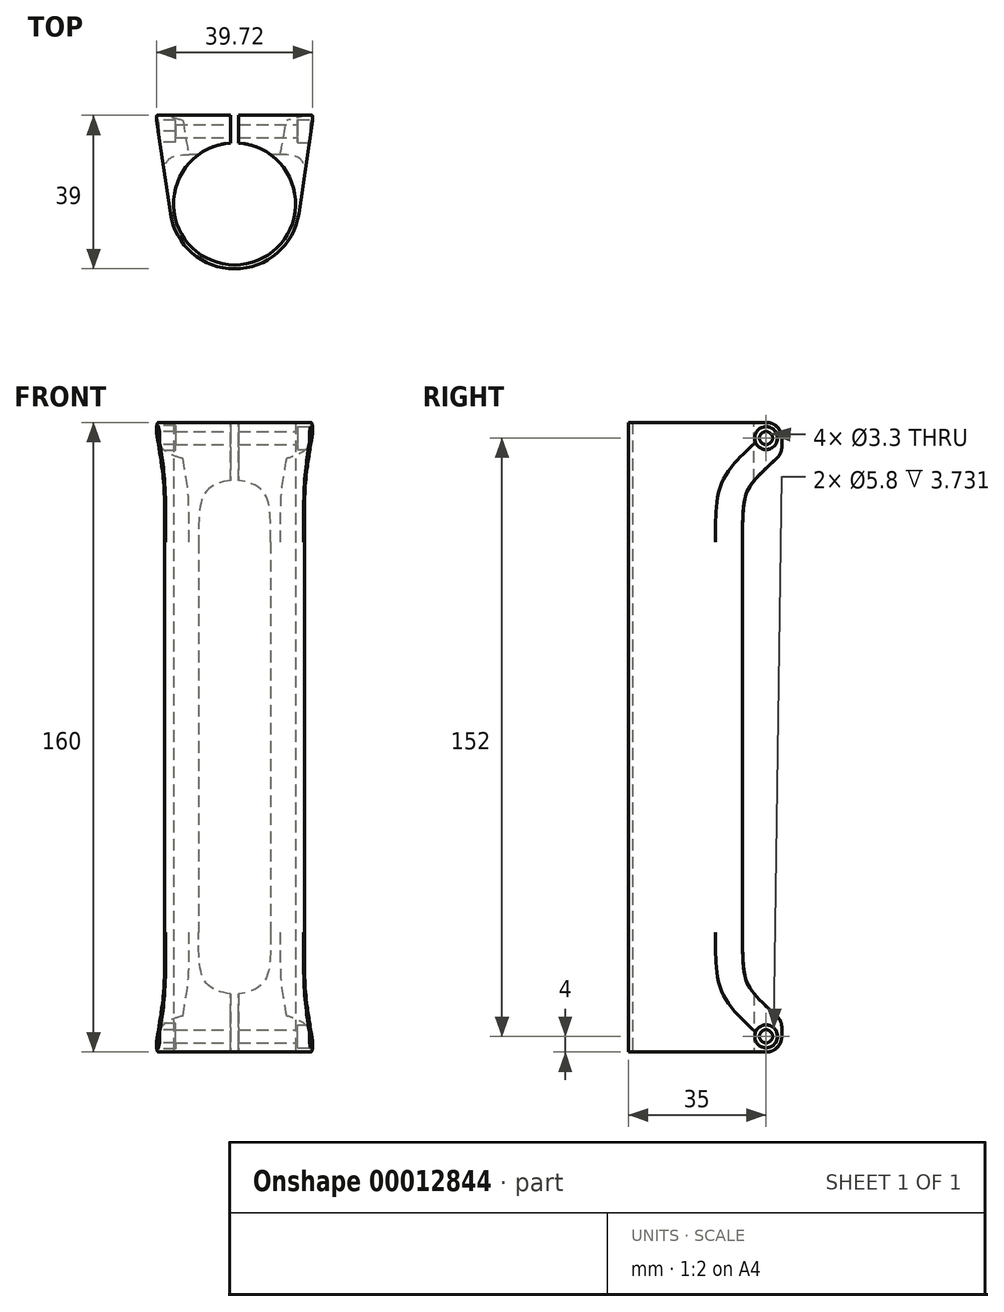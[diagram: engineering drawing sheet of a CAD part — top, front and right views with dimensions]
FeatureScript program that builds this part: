
annotation { "Feature Type Name" : "Feature", "Feature Type Description" : "" }
export const myFeature = defineFeature(function(context is Context, id is Id, definition is map)
    precondition{}
    {
        {
            var Q0;
            Q0=qCreatedBy(makeId("Top.planeOp"),FACE);
            var sketch = newSketch(context, id + "F0", { "sketchPlane" : qUnion([Q0])});
            skCircle(sketch, "E0", {"center": v(0, 0) * mm, "radius": 15.5 * mm});
            skSolve(sketch);
        }
        {
            var Q0;
            Q0=qCreatedBy(makeId("Top.planeOp"),FACE);
            var sketch = newSketch(context, id + "F1", { "sketchPlane" : qUnion([Q0])});
            skLineSegment(sketch, "E1", {"start": v(0, 22.5) * mm, "end": v(20, 22.5) * mm});
            skLineSegment(sketch, "E2", {"start": v(20, 22.5) * mm, "end": v(16.32, -2.4) * mm});
            skArc(sketch, "E3", {"start": v(0, -15.5) * mm, "mid": v(15.5, 0) * mm, "end": v(0, 15.5) * mm});
            skLineSegment(sketch, "E4", {"start": v(0, 15.5) * mm, "end": v(0, 22.5) * mm});
            skLineSegment(sketch, "E5", {"start": v(0, -15.5) * mm, "end": v(0, -16.5) * mm});
            skArc(sketch, "E6", {"start": v(0, -16.5) * mm, "mid": v(10.78, -12.5) * mm, "end": v(16.32, -2.4) * mm});
            skSolve(sketch);
        }
        {
            var Q0;
            Q0=makeQuery(id+"F1.imprint","IMPRINT",FACE,{"disambiguationData":[TD([[makeQuery(id+"F1.imprint","IMPRINT",EDGE,{"derivedFrom":sQuery(id+"F1.wireOp",EDGE,"E1")}),-1.0]])]});
            extrude(context, id + "F2", {"entities" : qUnion([Q0]), "depth" : 80 * mm});
        }
        {
            var Q0;
            Q0=makeQuery(id+"F2.opExtrude","SWEPT_BODY",BODY,{"disambiguationData":[OSD([sQuery(id+"F1.wireOp",EDGE,"E1"),sQuery(id+"F1.wireOp",EDGE,"E2"),sQuery(id+"F1.wireOp",EDGE,"6433310a-906e-4d0e-a87c-12e56682349a"),sQuery(id+"F1.wireOp",EDGE,"ec2daf9b-542c-445b-b6fd-9b136e921494"),sQuery(id+"F1.wireOp",EDGE,"E3"),sQuery(id+"F1.wireOp",EDGE,"E4")])]});
            var Q1;
            Q1=makeQuery(id+"F2.opExtrude","SWEPT_FACE",FACE,{"disambiguationData":[OSD([sQuery(id+"F1.wireOp",EDGE,"E4")])]});
            mirror(context, id + "F3", {"operationType" : NewBodyOperationType.ADD, "entities" : qUnion([Q0]), "mirrorPlane" : qUnion([Q1])});
        }
        {
            var Q0;
            Q0=qCreatedBy(makeId("Right.planeOp"),FACE);
            var sketch = newSketch(context, id + "F4", { "sketchPlane" : qUnion([Q0])});
            skLineSegment(sketch, "E7", {"start": v(22.5, 80) * mm, "end": v(22.5, 8) * mm});
            skLineSegment(sketch, "E8", {"start": v(12.5, 13.77) * mm, "end": v(12.5, 80) * mm});
            skLineSegment(sketch, "E9", {"start": v(22.5, 80) * mm, "end": v(12.5, 80) * mm});
            skLineSegment(sketch, "E10", {"start": v(15.5, 80) * mm, "end": v(15.5, 0) * mm, "construction": true});
            skLineSegment(sketch, "E11", {"start": v(12.5, 13.77) * mm, "end": v(22.5, 8) * mm});
            skSolve(sketch);
        }
        {
            var Q0;
            Q0=qSketchRegion(id+"F4",true);
            extrude(context, id + "F5", {"entities" : qUnion([Q0]), "operationType" : NewBodyOperationType.REMOVE, "endBound" : BoundingType.THROUGH_ALL, "oppositeDirection" : true, "depth" : 25 * mm, "hasSecondDirection" : true, "secondDirectionBound" : SecondDirectionBoundingType.THROUGH_ALL, "secondDirectionOppositeDirection" : false, "secondDirectionDepth" : 25 * mm});
        }
        {
            var Q0;
            Q0=makeQuery(id+"F5.boolean.opBoolean","COPY",EDGE,{"disambiguationData":[OD(1.0)],"derivedFrom":makeQuery(id+"F5.opExtrude","SWEPT_EDGE",EDGE,{"disambiguationData":[OSD([sQuery(id+"F4.wireOp",EDGE,"E8"),sQuery(id+"F4.wireOp",EDGE,"E11")])]})});
            fillet(context, id + "F6", {"entities" : qUnion([Q0]), "radius" : 30 * mm, "tangentPropagation" : true, "rho" : .75, "crossSection" : FilletCrossSection.CONIC, "allowEdgeOverflow" : false});
        }
        {
            var Q0;
            Q0=qCreatedBy(makeId("Right.planeOp"),FACE);
            var sketch = newSketch(context, id + "F7", { "sketchPlane" : qUnion([Q0])});
            skCircle(sketch, "E12", {"center": v(18.5, 4) * mm, "radius": 1.65 * mm});
            skLineSegment(sketch, "E13", {"start": v(18.5, 4) * mm, "end": v(18.5, 0) * mm, "construction": true});
            skLineSegment(sketch, "E14", {"start": v(18.5, 4) * mm, "end": v(22.5, 4) * mm, "construction": true});
            skLineSegment(sketch, "E15", {"start": v(18.5, 4) * mm, "end": v(12.5, 4) * mm, "construction": true});
            skSolve(sketch);
        }
        {
            var Q0;
            Q0=qSketchRegion(id+"F7",true);
            extrude(context, id + "F8", {"entities" : qUnion([Q0]), "operationType" : NewBodyOperationType.REMOVE, "endBound" : BoundingType.THROUGH_ALL, "oppositeDirection" : true, "depth" : 25 * mm, "hasSecondDirection" : true, "secondDirectionBound" : SecondDirectionBoundingType.THROUGH_ALL, "secondDirectionOppositeDirection" : false, "secondDirectionDepth" : 25 * mm});
        }
        {
            var Q0;
            Q0=qBodyType(qCreatedBy(id+"F10",EDGE),BodyType.WIRE);
            var Q1;
            Q1=qCreatedBy(makeId("Right.planeOp"),FACE);
            var Q2;
            Q2=makeQuery(id+"F2.opExtrude","CAP_VERTEX",VERTEX,{"disambiguationData":[OSD([sQuery(id+"F1.wireOp",EDGE,"E1"),sQuery(id+"F1.wireOp",EDGE,"E2")])],"isStart":true});
            cPlane(context, id + "F9", {"entities" : qUnion([Q0, Q1, Q2]), "cplaneType" : CPlaneType.PLANE_POINT, "offset" : 150 * mm, "width" : 150 * mm, "height" : 150 * mm});
        }
        {
            var Q0;
            Q0=qCreatedBy(id+"F9.planeOp",FACE);
            var sketch = newSketch(context, id + "F10", { "sketchPlane" : qUnion([Q0])});
            skCircle(sketch, "E16", {"center": v(18.5, 4) * mm, "radius": 2.9 * mm});
            skSolve(sketch);
        }
        {
            var Q0;
            Q0=qSketchRegion(id+"F10",true);
            extrude(context, id + "F11", {"entities" : qUnion([Q0]), "operationType" : NewBodyOperationType.REMOVE, "oppositeDirection" : true, "depth" : 4 * mm});
        }
        {
            var Q0;
            Q0=qBodyType(qCreatedBy(id+"F13",EDGE),BodyType.WIRE);
            var Q1;
            Q1=qCreatedBy(makeId("Right.planeOp"),FACE);
            var Q2;
            Q2=makeQuery(id+"F3.opPattern","COPY",VERTEX,{"derivedFrom":makeQuery(id+"F2.opExtrude","CAP_VERTEX",VERTEX,{"disambiguationData":[OSD([sQuery(id+"F1.wireOp",EDGE,"E1"),sQuery(id+"F1.wireOp",EDGE,"E2")])],"isStart":true}),"instanceName":"1"});
            cPlane(context, id + "F12", {"entities" : qUnion([Q0, Q1, Q2]), "cplaneType" : CPlaneType.PLANE_POINT, "offset" : 150 * mm, "width" : 150 * mm, "height" : 150 * mm});
        }
        {
            var Q0;
            Q0=qCreatedBy(id+"F12.planeOp",FACE);
            var sketch = newSketch(context, id + "F13", { "sketchPlane" : qUnion([Q0])});
            skLineSegment(sketch, "E17", {"start": v(15.7, 2.38) * mm, "end": v(15.7, 5.62) * mm});
            skLineSegment(sketch, "E18", {"start": v(15.7, 5.62) * mm, "end": v(18.5, 7.23) * mm});
            skLineSegment(sketch, "E19", {"start": v(18.5, 7.23) * mm, "end": v(21.3, 5.62) * mm});
            skLineSegment(sketch, "E20", {"start": v(21.3, 5.62) * mm, "end": v(21.3, 2.38) * mm});
            skLineSegment(sketch, "E21", {"start": v(21.3, 2.38) * mm, "end": v(18.5, 0.77) * mm});
            skLineSegment(sketch, "E22", {"start": v(18.5, 0.77) * mm, "end": v(15.7, 2.38) * mm});
            skCircle(sketch, "E23", {"center": v(18.5, 4) * mm, "radius": 3.23 * mm, "construction": true});
            skSolve(sketch);
        }
        {
            var Q0;
            Q0=makeQuery(id+"F13.imprint","IMPRINT",FACE,{"disambiguationData":[TD([[makeQuery(id+"F13.imprint","IMPRINT",EDGE,{"derivedFrom":sQuery(id+"F13.wireOp",EDGE,"E17")}),-1.0]])]});
            extrude(context, id + "F14", {"entities" : qUnion([Q0]), "operationType" : NewBodyOperationType.REMOVE, "depth" : 5 * mm});
        }
        {
            var Q0;
            {var subQ0=makeQuery(id+"F2.opExtrude","CAP_FACE",FACE,{"disambiguationData":[OSD([sQuery(id+"F1.wireOp",EDGE,"E1"),sQuery(id+"F1.wireOp",EDGE,"E2"),sQuery(id+"F1.wireOp",EDGE,"E3"),sQuery(id+"F1.wireOp",EDGE,"E4"),sQuery(id+"F1.wireOp",EDGE,"E5"),sQuery(id+"F1.wireOp",EDGE,"E6")])],"isStart":true});Q0=makeQuery(id+"F3.boolean.opBoolean","MERGE",FACE,{"derivedFrom":[subQ0,makeQuery(id+"F3.opPattern","COPY",FACE,{"derivedFrom":subQ0,"instanceName":"1"})]});}
            var sketch = newSketch(context, id + "F15", { "sketchPlane" : qUnion([Q0])});
            skLineSegment(sketch, "E24.bottom", {"start": v(1, -22.5) * mm, "end": v(-1, -22.5) * mm});
            skLineSegment(sketch, "E24.top", {"start": v(1, 0) * mm, "end": v(-1, 0) * mm});
            skLineSegment(sketch, "E24.left", {"start": v(1, -22.5) * mm, "end": v(1, 0) * mm});
            skLineSegment(sketch, "E24.right", {"start": v(-1, -22.5) * mm, "end": v(-1, 0) * mm});
            skSolve(sketch);
        }
        {
            var Q0;
            Q0=qSketchRegion(id+"F15",true);
            extrude(context, id + "F16", {"entities" : qUnion([Q0]), "operationType" : NewBodyOperationType.REMOVE, "endBound" : BoundingType.THROUGH_ALL, "oppositeDirection" : true, "depth" : 3 * mm});
        }
        {
            var Q0;
            Q0=makeQuery(id+"F5.boolean.opBoolean","INTERSECT",EDGE,{"derivedFrom":[makeQuery(id+"F2.opExtrude","SWEPT_FACE",FACE,{"disambiguationData":[OSD([sQuery(id+"F1.wireOp",EDGE,"E2")])]}),makeQuery(id+"F5.opExtrude","SWEPT_FACE",FACE,{"disambiguationData":[OSD([sQuery(id+"F4.wireOp",EDGE,"E8")])]})]});
            var Q1;
            Q1=makeQuery(id+"F5.boolean.opBoolean","INTERSECT",EDGE,{"derivedFrom":[makeQuery(id+"F3.opPattern","COPY",FACE,{"derivedFrom":makeQuery(id+"F2.opExtrude","SWEPT_FACE",FACE,{"disambiguationData":[OSD([sQuery(id+"F1.wireOp",EDGE,"E2")])]}),"instanceName":"1"}),makeQuery(id+"F5.opExtrude","SWEPT_FACE",FACE,{"disambiguationData":[OSD([sQuery(id+"F4.wireOp",EDGE,"E8")])]})]});
            fillet(context, id + "F17", {"entities" : qUnion([Q0, Q1]), "radius" : 6 * mm, "tangentPropagation" : true, "rho" : .6, "crossSection" : FilletCrossSection.CONIC, "allowEdgeOverflow" : false});
        }
        {
            var Q0;
            {var subQ0=sQuery(id+"F1.wireOp",EDGE,"E1");var subQ1=makeQuery(id+"F2.opExtrude","CAP_EDGE",EDGE,{"disambiguationData":[OSD([subQ0])],"isStart":true});var subQ2=sQuery(id+"F1.wireOp",EDGE,"E2");Q0=makeQuery(id+"F16.boolean.opBoolean","SPLIT",EDGE,{"disambiguationData":[TD([makeQuery(id+"F3.opPattern","COPY",FACE,{"derivedFrom":makeQuery(id+"F2.opExtrude","SWEPT_FACE",FACE,{"disambiguationData":[OSD([subQ2])]}),"instanceName":"1"})])],"derivedFrom":makeQuery(id+"F3.boolean.opBoolean","MERGE",EDGE,{"derivedFrom":[subQ1,makeQuery(id+"F3.opPattern","COPY",EDGE,{"derivedFrom":subQ1,"instanceName":"1"})]})});}
            var Q1;
            {var subQ0=sQuery(id+"F1.wireOp",EDGE,"E1");var subQ1=makeQuery(id+"F2.opExtrude","CAP_EDGE",EDGE,{"disambiguationData":[OSD([subQ0])],"isStart":true});var subQ3=sQuery(id+"F1.wireOp",EDGE,"E2");Q1=makeQuery(id+"F16.boolean.opBoolean","SPLIT",EDGE,{"disambiguationData":[TD([makeQuery(id+"F2.opExtrude","SWEPT_FACE",FACE,{"disambiguationData":[OSD([subQ3])]})])],"derivedFrom":makeQuery(id+"F3.boolean.opBoolean","MERGE",EDGE,{"derivedFrom":[subQ1,makeQuery(id+"F3.opPattern","COPY",EDGE,{"derivedFrom":subQ1,"instanceName":"1"})]})});}
            var Q2;
            {var subQ0=sQuery(id+"F4.wireOp",EDGE,"E8");var subQ1=sQuery(id+"F4.wireOp",EDGE,"E11");var subQ2=makeQuery(id+"F2.opExtrude","SWEPT_FACE",FACE,{"disambiguationData":[OSD([sQuery(id+"F1.wireOp",EDGE,"E1")])]});var subQ3=makeQuery(id+"F3.opPattern","COPY",FACE,{"derivedFrom":subQ2,"instanceName":"1"});Q2=makeQuery(id+"F16.boolean.opBoolean","SPLIT",EDGE,{"disambiguationData":[TD([makeQuery(id+"F2.opExtrude","SWEPT_FACE",FACE,{"disambiguationData":[OSD([sQuery(id+"F1.wireOp",EDGE,"E2")])]})])],"derivedFrom":makeQuery(id+"F6.opFillet","BLEND_EDGE",EDGE,{"blendedFrom":[makeQuery(id+"F5.boolean.opBoolean","COPY",EDGE,{"disambiguationData":[OD(1.0)],"derivedFrom":makeQuery(id+"F5.opExtrude","SWEPT_EDGE",EDGE,{"disambiguationData":[OSD([subQ0,subQ1])]})}),makeQuery(id+"F3.boolean.opBoolean","MERGE",FACE,{"derivedFrom":[subQ2,subQ3]})],"blendedInto":[makeQuery(id+"F3.boolean.opBoolean","MERGE",FACE,{"derivedFrom":[subQ2,subQ3]})]})});}
            var Q3;
            {var subQ0=sQuery(id+"F4.wireOp",EDGE,"E8");var subQ1=sQuery(id+"F4.wireOp",EDGE,"E11");var subQ2=makeQuery(id+"F2.opExtrude","SWEPT_FACE",FACE,{"disambiguationData":[OSD([sQuery(id+"F1.wireOp",EDGE,"E1")])]});var subQ3=makeQuery(id+"F3.opPattern","COPY",FACE,{"derivedFrom":subQ2,"instanceName":"1"});Q3=makeQuery(id+"F16.boolean.opBoolean","SPLIT",EDGE,{"disambiguationData":[TD([makeQuery(id+"F3.opPattern","COPY",FACE,{"derivedFrom":makeQuery(id+"F2.opExtrude","SWEPT_FACE",FACE,{"disambiguationData":[OSD([sQuery(id+"F1.wireOp",EDGE,"E2")])]}),"instanceName":"1"})])],"derivedFrom":makeQuery(id+"F6.opFillet","BLEND_EDGE",EDGE,{"blendedFrom":[makeQuery(id+"F5.boolean.opBoolean","COPY",EDGE,{"disambiguationData":[OD(1.0)],"derivedFrom":makeQuery(id+"F5.opExtrude","SWEPT_EDGE",EDGE,{"disambiguationData":[OSD([subQ0,subQ1])]})}),makeQuery(id+"F3.boolean.opBoolean","MERGE",FACE,{"derivedFrom":[subQ2,subQ3]})],"blendedInto":[makeQuery(id+"F3.boolean.opBoolean","MERGE",FACE,{"derivedFrom":[subQ2,subQ3]})]})});}
            fillet(context, id + "F18", {"entities" : qUnion([Q0, Q1, Q2, Q3]), "radius" : 4 * mm, "allowEdgeOverflow" : false});
        }
        {
            var Q0;
            Q0=makeQuery(id+"F2.opExtrude","SWEPT_BODY",BODY,{"disambiguationData":[OSD([sQuery(id+"F1.wireOp",EDGE,"E1"),sQuery(id+"F1.wireOp",EDGE,"E2"),sQuery(id+"F1.wireOp",EDGE,"6433310a-906e-4d0e-a87c-12e56682349a"),sQuery(id+"F1.wireOp",EDGE,"ec2daf9b-542c-445b-b6fd-9b136e921494"),sQuery(id+"F1.wireOp",EDGE,"E3"),sQuery(id+"F1.wireOp",EDGE,"E4")])]});
            var Q1;
            {var subQ0=sQuery(id+"F1.wireOp",EDGE,"E2");var subQ1=sQuery(id+"F1.wireOp",EDGE,"6433310a-906e-4d0e-a87c-12e56682349a");var subQ2=sQuery(id+"F1.wireOp",EDGE,"ec2daf9b-542c-445b-b6fd-9b136e921494");var subQ3=sQuery(id+"F1.wireOp",EDGE,"E3");var subQ4=makeQuery(id+"F2.opExtrude","CAP_FACE",FACE,{"disambiguationData":[OSD([sQuery(id+"F1.wireOp",EDGE,"E1"),subQ0,subQ1,subQ2,subQ3,sQuery(id+"F1.wireOp",EDGE,"E4")])],"isStart":false});var subQ6=makeQuery(id+"F2.opExtrude","SWEPT_FACE",FACE,{"disambiguationData":[OSD([subQ1])]});Q1=makeQuery(id+"F5.boolean.opBoolean","SPLIT",FACE,{"disambiguationData":[TD([subQ6])],"derivedFrom":makeQuery(id+"F3.boolean.opBoolean","MERGE",FACE,{"derivedFrom":[subQ4,makeQuery(id+"F3.opPattern","COPY",FACE,{"derivedFrom":subQ4,"instanceName":"1"})]})});}
            mirror(context, id + "F19", {"operationType" : NewBodyOperationType.ADD, "entities" : qUnion([Q0]), "mirrorPlane" : qUnion([Q1])});
        }
    });
